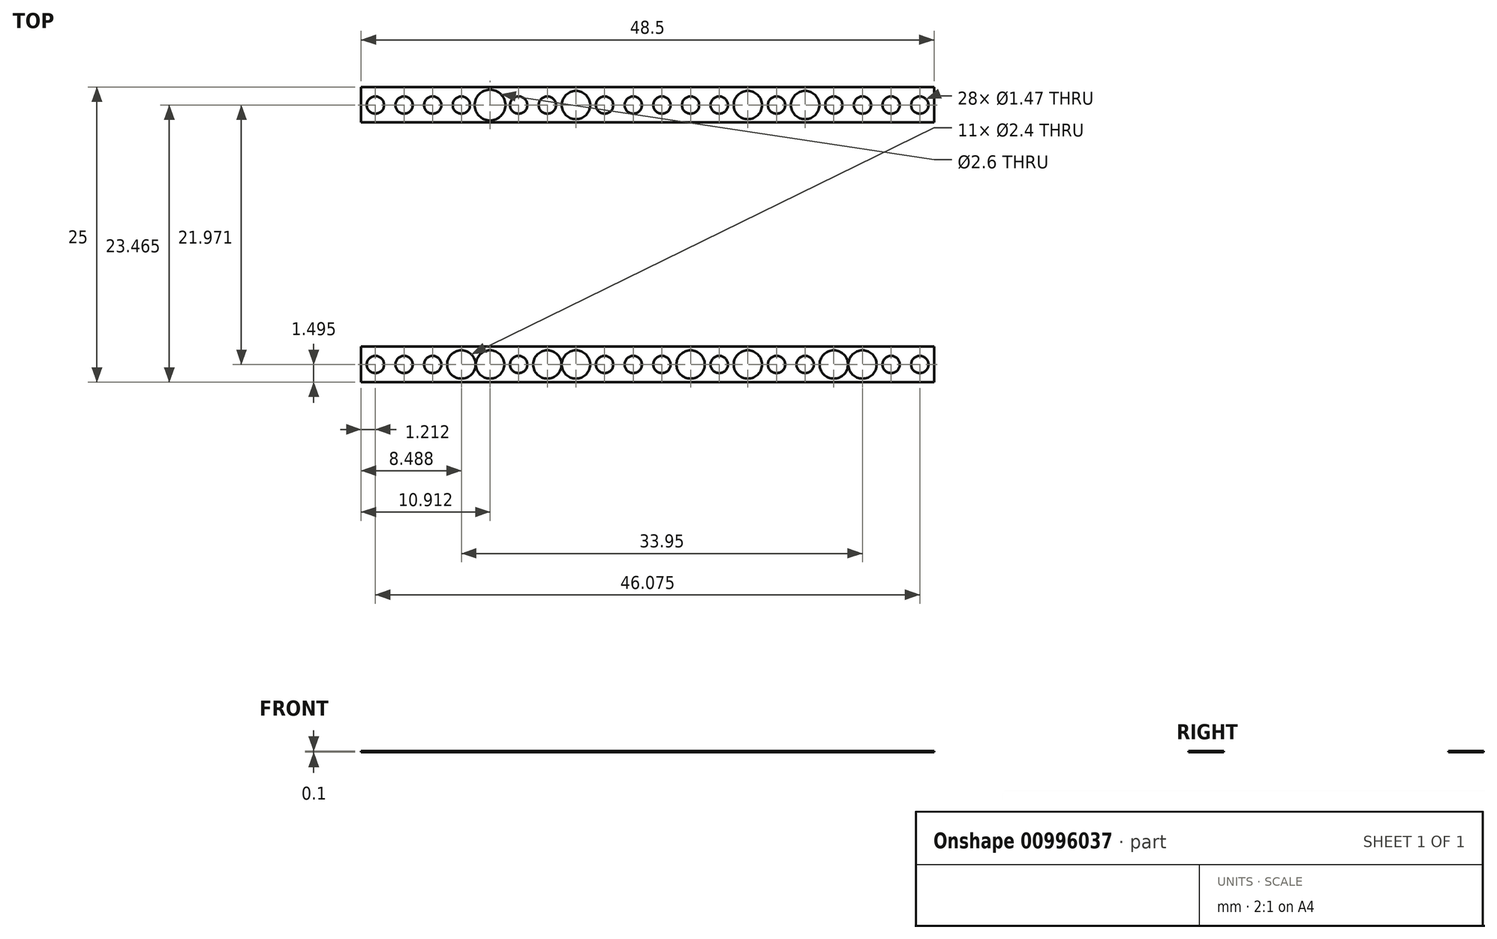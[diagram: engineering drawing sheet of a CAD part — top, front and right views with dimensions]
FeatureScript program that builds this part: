
annotation { "Feature Type Name" : "Feature", "Feature Type Description" : "" }
export const myFeature = defineFeature(function(context is Context, id is Id, definition is map)
    precondition{}
    {
        {
            var Q0;
            Q0=qCreatedBy(makeId("Top.planeOp"),FACE);
            var sketch = newSketch(context, id + "F0", { "sketchPlane" : qUnion([Q0])});
            skLineSegment(sketch, "E0.bottom", {"start": v(-24.25, 14.5) * mm, "end": v(24.25, 14.5) * mm});
            skLineSegment(sketch, "E0.top", {"start": v(-24.25, -14.5) * mm, "end": v(24.25, -14.5) * mm});
            skLineSegment(sketch, "E0.left", {"start": v(-24.25, 14.5) * mm, "end": v(-24.25, -14.5) * mm});
            skLineSegment(sketch, "E0.right", {"start": v(24.25, 14.5) * mm, "end": v(24.25, -14.5) * mm});
            skPoint(sketch, "E0.middle", {"position": v(0, 0) * mm});
            skLineSegment(sketch, "E1", {"start": v(-24.25, -10.5) * mm, "end": v(24.25, -10.5) * mm});
            skLineSegment(sketch, "E2", {"start": v(24.25, -7.5) * mm, "end": v(-24.25, -7.5) * mm});
            skLineSegment(sketch, "E3", {"start": v(24.25, 11.5) * mm, "end": v(-24.25, 11.5) * mm});
            skLineSegment(sketch, "E4", {"start": v(1.06, -7.5) * mm, "end": v(1.06, 11.5) * mm});
            skLineSegment(sketch, "E5", {"start": v(-1.18, -7.5) * mm, "end": v(-1.18, 11.5) * mm});
            skLineSegment(sketch, "E6", {"start": v(0, -10.5) * mm, "end": v(0, 14.5) * mm, "construction": true});
            skCircle(sketch, "E7", {"center": v(23.04, -9) * mm, "radius": 0.73 * mm});
            skCircle(sketch, "E8", {"center": v(20.61, -9) * mm, "radius": 0.73 * mm});
            skCircle(sketch, "E9", {"center": v(18.19, -9) * mm, "radius": 0.73 * mm});
            skCircle(sketch, "E10", {"center": v(15.76, -9) * mm, "radius": 0.73 * mm});
            skCircle(sketch, "E11", {"center": v(13.34, -9) * mm, "radius": 0.73 * mm});
            skCircle(sketch, "E12", {"center": v(10.91, -9) * mm, "radius": 0.73 * mm});
            skCircle(sketch, "E13", {"center": v(8.49, -9) * mm, "radius": 0.73 * mm});
            skCircle(sketch, "E14", {"center": v(6.06, -9) * mm, "radius": 0.73 * mm});
            skCircle(sketch, "E15", {"center": v(3.64, -9) * mm, "radius": 0.73 * mm});
            skCircle(sketch, "E16", {"center": v(1.21, -9) * mm, "radius": 0.73 * mm});
            skLineSegment(sketch, "E17", {"start": v(24.25, -9) * mm, "end": v(-24.25, -9) * mm, "construction": true});
            skCircle(sketch, "E18", {"center": v(-1.21, -9) * mm, "radius": 0.73 * mm});
            skCircle(sketch, "E19", {"center": v(-3.64, -9) * mm, "radius": 0.73 * mm});
            skCircle(sketch, "E20", {"center": v(-6.06, -9) * mm, "radius": 0.73 * mm});
            skCircle(sketch, "E21", {"center": v(-8.49, -9) * mm, "radius": 0.73 * mm});
            skCircle(sketch, "E22", {"center": v(-10.91, -9) * mm, "radius": 0.73 * mm});
            skCircle(sketch, "E23", {"center": v(-13.34, -9) * mm, "radius": 0.73 * mm});
            skCircle(sketch, "E24", {"center": v(-15.76, -9) * mm, "radius": 0.73 * mm});
            skCircle(sketch, "E25", {"center": v(-18.19, -9) * mm, "radius": 0.73 * mm});
            skCircle(sketch, "E26", {"center": v(-20.61, -9) * mm, "radius": 0.73 * mm});
            skCircle(sketch, "E27", {"center": v(-23.04, -9) * mm, "radius": 0.73 * mm});
            skLineSegment(sketch, "E28", {"start": v(24.25, 12.97) * mm, "end": v(-24.25, 12.97) * mm, "construction": true});
            skCircle(sketch, "E29", {"center": v(23.04, 12.97) * mm, "radius": 0.73 * mm});
            skCircle(sketch, "E30", {"center": v(20.61, 12.97) * mm, "radius": 0.73 * mm});
            skCircle(sketch, "E31", {"center": v(18.19, 12.97) * mm, "radius": 0.73 * mm});
            skCircle(sketch, "E32", {"center": v(15.76, 12.97) * mm, "radius": 0.73 * mm});
            skCircle(sketch, "E33", {"center": v(13.34, 12.97) * mm, "radius": 0.73 * mm});
            skCircle(sketch, "E34", {"center": v(10.91, 12.97) * mm, "radius": 0.73 * mm});
            skCircle(sketch, "E35", {"center": v(8.49, 12.97) * mm, "radius": 0.73 * mm});
            skCircle(sketch, "E36", {"center": v(6.06, 12.97) * mm, "radius": 0.73 * mm});
            skCircle(sketch, "E37", {"center": v(3.64, 12.97) * mm, "radius": 0.73 * mm});
            skCircle(sketch, "E38", {"center": v(1.21, 12.97) * mm, "radius": 0.73 * mm});
            skCircle(sketch, "E39", {"center": v(-1.21, 12.97) * mm, "radius": 0.73 * mm});
            skCircle(sketch, "E40", {"center": v(-3.64, 12.97) * mm, "radius": 0.73 * mm});
            skCircle(sketch, "E41", {"center": v(-6.06, 12.97) * mm, "radius": 0.73 * mm});
            skCircle(sketch, "E42", {"center": v(-8.49, 12.97) * mm, "radius": 0.73 * mm});
            skCircle(sketch, "E43", {"center": v(-10.91, 12.97) * mm, "radius": 0.73 * mm});
            skCircle(sketch, "E44", {"center": v(-13.34, 12.97) * mm, "radius": 0.73 * mm});
            skCircle(sketch, "E45", {"center": v(-15.76, 12.97) * mm, "radius": 0.73 * mm});
            skCircle(sketch, "E46", {"center": v(-18.19, 12.97) * mm, "radius": 0.73 * mm});
            skCircle(sketch, "E47", {"center": v(-20.61, 12.97) * mm, "radius": 0.73 * mm});
            skCircle(sketch, "E48", {"center": v(-23.04, 12.97) * mm, "radius": 0.73 * mm});
            skLineSegment(sketch, "E49.bottom", {"start": v(-24.25, -7.5) * mm, "end": v(-23.1, -7.5) * mm});
            skLineSegment(sketch, "E49.top", {"start": v(-24.25, 11.5) * mm, "end": v(-23.1, 11.5) * mm});
            skLineSegment(sketch, "E49.left", {"start": v(-24.25, -7.5) * mm, "end": v(-24.25, 11.5) * mm});
            skLineSegment(sketch, "E49.right", {"start": v(-23.1, -7.5) * mm, "end": v(-23.1, 11.5) * mm});
            skCircle(sketch, "E50", {"center": v(-13.34, 12.97) * mm, "radius": 1.3 * mm});
            skCircle(sketch, "E51", {"center": v(-6.06, 12.97) * mm, "radius": 1.2 * mm});
            skCircle(sketch, "E52", {"center": v(-15.76, -9) * mm, "radius": 1.2 * mm});
            skCircle(sketch, "E53", {"center": v(-13.34, -9) * mm, "radius": 1.2 * mm});
            skCircle(sketch, "E54", {"center": v(-8.49, -9) * mm, "radius": 1.2 * mm});
            skCircle(sketch, "E55", {"center": v(-6.06, -9) * mm, "radius": 1.2 * mm});
            skCircle(sketch, "E56", {"center": v(3.64, -9) * mm, "radius": 1.2 * mm});
            skCircle(sketch, "E57", {"center": v(8.49, -9) * mm, "radius": 1.2 * mm});
            skCircle(sketch, "E58", {"center": v(15.76, -9) * mm, "radius": 1.2 * mm});
            skCircle(sketch, "E59", {"center": v(18.19, -9) * mm, "radius": 1.2 * mm});
            skCircle(sketch, "E60", {"center": v(13.34, 12.97) * mm, "radius": 1.2 * mm});
            skCircle(sketch, "E61", {"center": v(8.49, 12.97) * mm, "radius": 1.2 * mm});
            skSolve(sketch);
        }
        {
            var Q0;
            Q0=makeQuery(id+"F0.imprint","IMPRINT",FACE,{"disambiguationData":[TD([[makeQuery(id+"F0.imprint","IMPRINT",EDGE,{"derivedFrom":sQuery(id+"F0.wireOp",EDGE,"E0.bottom")}),-1.0]])]});
            var Q1;
            {var subQ0=sQuery(id+"F0.wireOp",EDGE,"E1");Q1=makeQuery(id+"F0.imprint","IMPRINT",FACE,{"disambiguationData":[TD([[makeQuery(id+"F0.imprint","IMPRINT",EDGE,{"derivedFrom":subQ0}),1.0]])]});}
            var Q2;
            {var subQ0=sQuery(id+"F0.wireOp",EDGE,"5GrS0vse-9AJ3-ZVxg-0uHS-31047rAuu6rO");Q2=makeQuery(id+"F0.imprint","IMPRINT",FACE,{"disambiguationData":[TD([[makeQuery(id+"F0.imprint","IMPRINT",EDGE,{"derivedFrom":subQ0}),-1.0]])]});}
            var Q3;
            {var subQ0=sQuery(id+"F0.wireOp",EDGE,"5GrS0vse-9AJ3-ZVxg-0uHS-31047rAuu6rO");Q3=makeQuery(id+"F0.imprint","IMPRINT",FACE,{"disambiguationData":[TD([[makeQuery(id+"F0.imprint","IMPRINT",EDGE,{"derivedFrom":subQ0}),1.0]])]});}
            var Q4;
            Q4=makeQuery(id+"F0.imprint","IMPRINT",FACE,{"disambiguationData":[TD([[makeQuery(id+"F0.imprint","IMPRINT",EDGE,{"derivedFrom":sQuery(id+"F0.wireOp",EDGE,"E49.bottom")}),1.0]])]});
            extrude(context, id + "F1", {"entities" : qUnion([Q0, Q1, Q2, Q3, Q4]), "depth" : 0.1 * mm, "offsetDistance" : 25 * mm});
        }
    });
